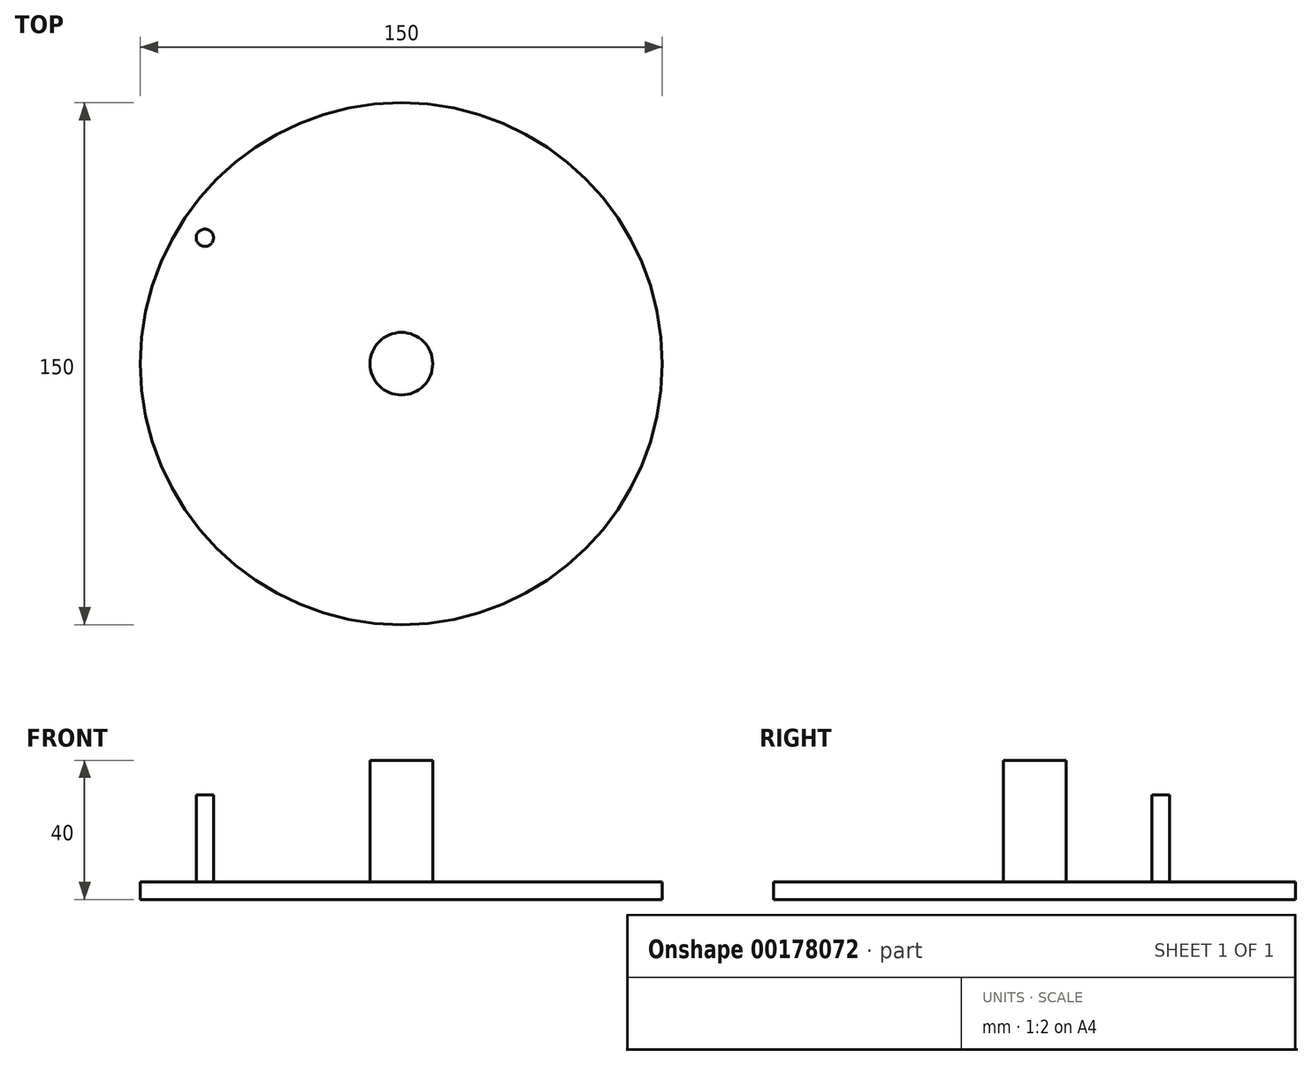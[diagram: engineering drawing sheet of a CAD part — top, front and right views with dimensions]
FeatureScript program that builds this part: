
annotation { "Feature Type Name" : "Feature", "Feature Type Description" : "" }
export const myFeature = defineFeature(function(context is Context, id is Id, definition is map)
    precondition{}
    {
        {
            var Q0;
            Q0=qCreatedBy(makeId("Top.planeOp"),FACE);
            var sketch = newSketch(context, id + "F0", { "sketchPlane" : qUnion([Q0])});
            skCircle(sketch, "E0", {"center": v(0, 0) * mm, "radius": 9 * mm});
            skSolve(sketch);
        }
        {
            var Q0;
            Q0 = qSketchRegion(id + "F0", true);
            extrude(context, id + "F1", {"entities" : qUnion([Q0]), "depth" : 40 * mm});
        }
        {
            var Q0;
            Q0=qCreatedBy(makeId("Top.planeOp"),FACE);
            var sketch = newSketch(context, id + "F2", { "sketchPlane" : qUnion([Q0])});
            skCircle(sketch, "E1", {"center": v(0, 0) * mm, "radius": 75 * mm});
            skSolve(sketch);
        }
        {
            var Q0;
            Q0 = qSketchRegion(id + "F2", true);
            extrude(context, id + "F3", {"entities" : qUnion([Q0]), "operationType" : NewBodyOperationType.ADD, "depth" : 5 * mm});
        }
        {
            var Q0;
            Q0=makeQuery(id+"F3.opExtrude","CAP_FACE",FACE,{"disambiguationData":[OSD([sQuery(id+"F2.wireOp",EDGE,"E1")])],"isStart":false});
            var sketch = newSketch(context, id + "F4", { "sketchPlane" : qUnion([Q0])});
            skCircle(sketch, "E2", {"center": v(-56.47, 36.2) * mm, "radius": 2.5 * mm});
            skSolve(sketch);
        }
        {
            var Q0;
            Q0 = qSketchRegion(id + "F4", true);
            extrude(context, id + "F5", {"entities" : qUnion([Q0]), "operationType" : NewBodyOperationType.ADD, "depth" : 25 * mm});
        }
    });
